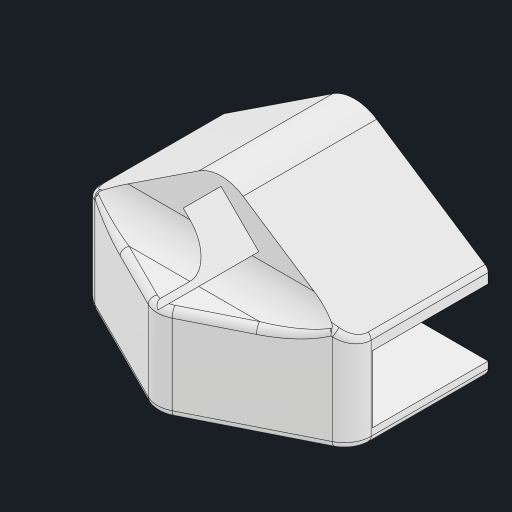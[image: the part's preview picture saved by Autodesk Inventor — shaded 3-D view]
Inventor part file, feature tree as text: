
AUTODESK INVENTOR PART (.ipt)
format: ipt  version: 2023 (Build 270158000, 158)  size: 266,752 bytes
history: native  units: mm
features: extrude x5, sketch x5, projected_geometry x5, fillet x3, other x2
ambient origin geometry x8: Origin, YZ Plane, XZ Plane, XY Plane, X Axis, Y Axis, Z Axis, Center Point
bodies: Body1 (feature_tree)
feature tree (20):
  other  "ソリッド1"
  extrude  "押し出し1"  Depth=20.0mm
  extrude  "押し出し2"  Depth=5.0mm
  extrude  "押し出し3"  Depth=15.0mm
  extrude  "押し出し4"  Depth=1.0mm TaperAngle=0.0deg
  fillet  "フィレット2"  Radius=300.0mm
  fillet  "フィレット3"  Radius=50.0mm
  fillet  "フィレット4"  Radius=3.0mm
  extrude  "押し出し5"  Depth=5.0mm TaperAngle=0.0deg
  other  "作業平面1"
  sketch  "スケッチ1"
  sketch  "スケッチ2"
  projected_geometry  "投影ループ1"
  sketch  "スケッチ3"
  projected_geometry  "投影ループ2"
  projected_geometry  "投影ループ3"
  sketch  "スケッチ4"
  projected_geometry  "投影ループ4"
  sketch  "スケッチ5"
  projected_geometry  "投影ループ5"
